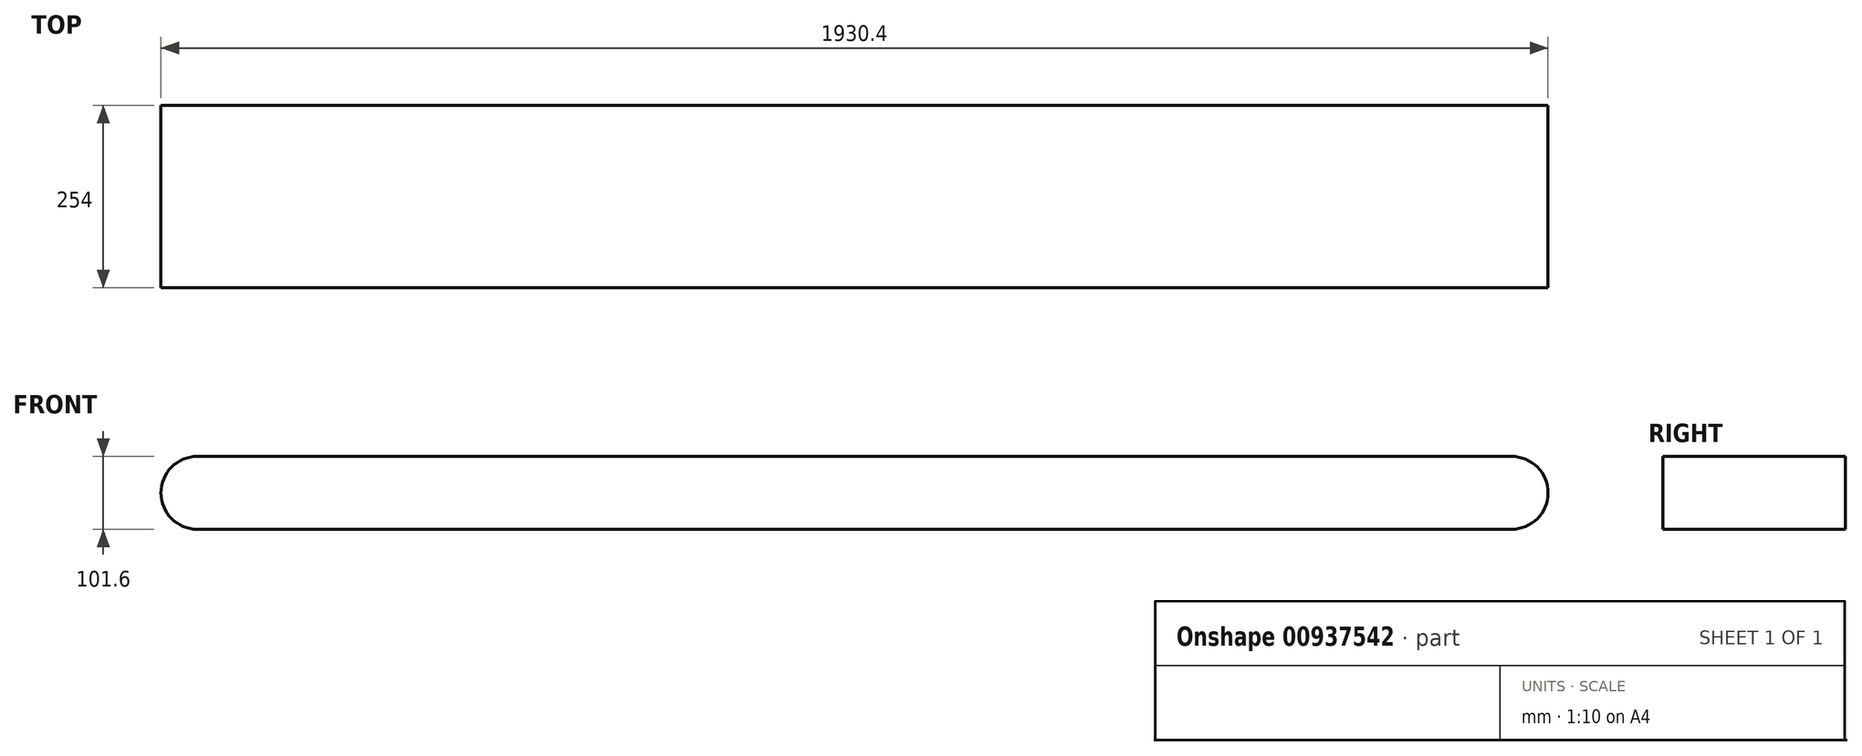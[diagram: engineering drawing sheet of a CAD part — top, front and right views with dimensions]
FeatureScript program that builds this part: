
annotation { "Feature Type Name" : "Feature", "Feature Type Description" : "" }
export const myFeature = defineFeature(function(context is Context, id is Id, definition is map)
    precondition{}
    {
        {
            var Q0;
            Q0=qCreatedBy(makeId("Front.planeOp"),FACE);
            var sketch = newSketch(context, id + "F0", { "sketchPlane" : qUnion([Q0])});
            skLineSegment(sketch, "E0", {"start": v(-914.4, 0) * mm, "end": v(914.4, 0) * mm, "construction": true});
            skLineSegment(sketch, "E1.0", {"start": v(-914.4, -50.8) * mm, "end": v(914.4, -50.8) * mm});
            skLineSegment(sketch, "E2.0", {"start": v(-914.4, 50.8) * mm, "end": v(914.4, 50.8) * mm});
            skCircle(sketch, "E3", {"center": v(-914.4, 0) * mm, "radius": 50.8 * mm});
            skCircle(sketch, "E4", {"center": v(914.4, 0) * mm, "radius": 50.8 * mm});
            skSolve(sketch);
        }
        {
            var Q0;
            {var subQ0=sQuery(id+"F0.wireOp",EDGE,"E3");var subQ1=makeQuery(id+"F0.imprint","INTERSECT",VERTEX,{"derivedFrom":[sQuery(id+"F0.wireOp",EDGE,"E1.0"),subQ0]});Q0=makeQuery(id+"F0.imprint","IMPRINT",FACE,{"disambiguationData":[TD([[makeQuery(id+"F0.imprint","IMPRINT",EDGE,{"disambiguationData":[TD([[subQ1,1.0]])],"derivedFrom":subQ0}),1.0]])]});}
            var Q1;
            {var subQ0=sQuery(id+"F0.wireOp",EDGE,"E4");var subQ1=makeQuery(id+"F0.imprint","INTERSECT",VERTEX,{"derivedFrom":[sQuery(id+"F0.wireOp",EDGE,"E1.0"),subQ0]});Q1=makeQuery(id+"F0.imprint","IMPRINT",FACE,{"disambiguationData":[TD([[makeQuery(id+"F0.imprint","IMPRINT",EDGE,{"disambiguationData":[TD([[subQ1,1.0]])],"derivedFrom":subQ0}),1.0]])]});}
            var Q2;
            {var subQ0=sQuery(id+"F0.wireOp",EDGE,"E1.0");Q2=makeQuery(id+"F0.imprint","IMPRINT",FACE,{"disambiguationData":[TD([[makeQuery(id+"F0.imprint","IMPRINT",EDGE,{"derivedFrom":subQ0}),1.0]])]});}
            extrude(context, id + "F1", {"entities" : qUnion([Q0, Q1, Q2]), "depth" : 254 * mm, "offsetDistance" : 25.4 * mm});
        }
    });
